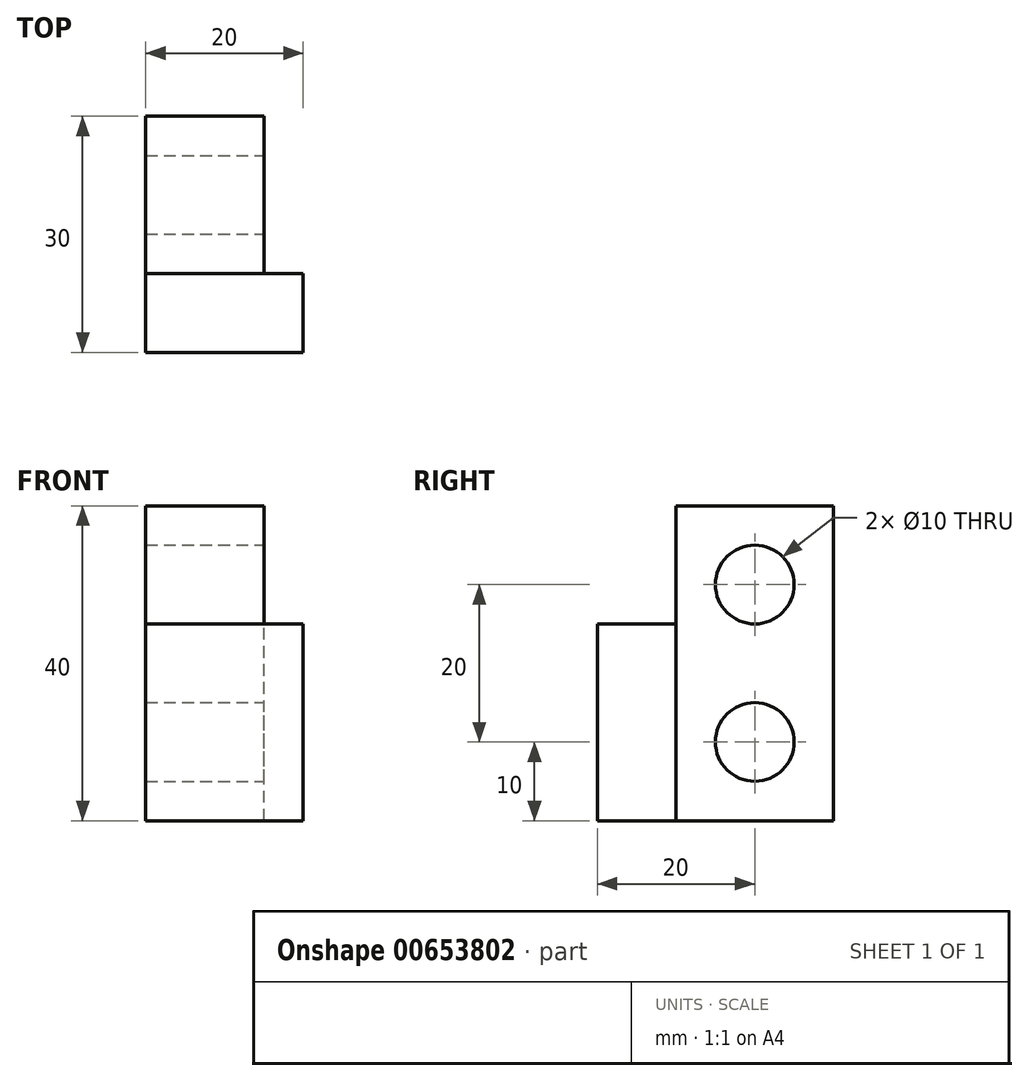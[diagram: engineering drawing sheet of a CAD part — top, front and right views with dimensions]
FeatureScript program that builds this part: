
annotation { "Feature Type Name" : "Feature", "Feature Type Description" : "" }
export const myFeature = defineFeature(function(context is Context, id is Id, definition is map)
    precondition{}
    {
        {
            var Q0;
            Q0=qCreatedBy(makeId("Right.planeOp"),FACE);
            var sketch = newSketch(context, id + "F0", { "sketchPlane" : qUnion([Q0])});
            skLineSegment(sketch, "E0.bottom", {"start": v(0, 0) * mm, "end": v(-20, 0) * mm});
            skLineSegment(sketch, "E0.top", {"start": v(0, 40) * mm, "end": v(-20, 40) * mm});
            skLineSegment(sketch, "E0.left", {"start": v(0, 0) * mm, "end": v(0, 40) * mm});
            skLineSegment(sketch, "E0.right", {"start": v(-20, 0) * mm, "end": v(-20, 40) * mm});
            skCircle(sketch, "E1", {"center": v(-10, 10) * mm, "radius": 5 * mm});
            skPoint(sketch, "E1.centerSnap0", {"position": v(-18.13, 10) * mm});
            skLineSegment(sketch, "E2.bottom", {"start": v(-20, 0) * mm, "end": v(-30, 0) * mm});
            skLineSegment(sketch, "E2.top", {"start": v(-20, 25) * mm, "end": v(-30, 25) * mm});
            skLineSegment(sketch, "E2.left", {"start": v(-20, 0) * mm, "end": v(-20, 25) * mm});
            skLineSegment(sketch, "E2.right", {"start": v(-30, 0) * mm, "end": v(-30, 25) * mm});
            skSolve(sketch);
        }
        {
            var Q0;
            Q0=makeQuery(id+"F0.imprint","IMPRINT",FACE,{"disambiguationData":[TD([[makeQuery(id+"F0.imprint","IMPRINT",EDGE,{"derivedFrom":sQuery(id+"F0.wireOp",EDGE,"E0.bottom")}),-1.0]])]});
            extrude(context, id + "F1", {"entities" : qUnion([Q0]), "depth" : 15 * mm, "offsetDistance" : 25.4 * mm});
        }
        {
            var Q0;
            Q0=makeQuery(id+"F0.imprint","IMPRINT",FACE,{"disambiguationData":[TD([[makeQuery(id+"F0.imprint","IMPRINT",EDGE,{"derivedFrom":sQuery(id+"F0.wireOp",EDGE,"E2.bottom")}),-1.0]])]});
            var Q1;
            Q1=makeQuery(id+"F0.imprint","IMPRINT",FACE,{"disambiguationData":[TD([[makeQuery(id+"F0.imprint","IMPRINT",EDGE,{"derivedFrom":sQuery(id+"F0.wireOp",EDGE,"E1")}),1.0]])]});
            extrude(context, id + "F2", {"entities" : qUnion([Q0, Q1]), "operationType" : NewBodyOperationType.ADD, "depth" : 20 * mm, "offsetDistance" : 25.4 * mm});
        }
        {
            var Q0;
            Q0=makeQuery(id+"F1.opExtrude","CAP_FACE",FACE,{"disambiguationData":[OSD([sQuery(id+"F0.wireOp",EDGE,"E0.bottom"),sQuery(id+"F0.wireOp",EDGE,"E0.top"),sQuery(id+"F0.wireOp",EDGE,"E0.left"),sQuery(id+"F0.wireOp",EDGE,"E0.right"),sQuery(id+"F0.wireOp",EDGE,"E1"),sQuery(id+"F0.wireOp",EDGE,"E2.left")])],"isStart":false});
            var sketch = newSketch(context, id + "F3", { "sketchPlane" : qUnion([Q0])});
            skCircle(sketch, "E3", {"center": v(-10, 30) * mm, "radius": 5 * mm});
            skSolve(sketch);
        }
        {
            var Q0;
            Q0=makeQuery(id+"F2.opExtrude","CAP_FACE",FACE,{"disambiguationData":[OSD([sQuery(id+"F0.wireOp",EDGE,"E1")])],"isStart":false});
            var Q1;
            {var subQ0=sQuery(id+"F0.wireOp",EDGE,"E2.left");var subQ1=sQuery(id+"F0.wireOp",EDGE,"E1");Q1=makeQuery(id+"F2.boolean.opBoolean","MERGE",FACE,{"derivedFrom":[makeQuery(id+"F1.opExtrude","CAP_FACE",FACE,{"disambiguationData":[OSD([sQuery(id+"F0.wireOp",EDGE,"E0.bottom"),sQuery(id+"F0.wireOp",EDGE,"E0.top"),sQuery(id+"F0.wireOp",EDGE,"E0.left"),sQuery(id+"F0.wireOp",EDGE,"E0.right"),subQ1,subQ0])],"isStart":true}),makeQuery(id+"F2.opExtrude","CAP_FACE",FACE,{"disambiguationData":[OSD([subQ1])],"isStart":true}),makeQuery(id+"F2.opExtrude","CAP_FACE",FACE,{"disambiguationData":[OSD([sQuery(id+"F0.wireOp",EDGE,"E2.bottom"),sQuery(id+"F0.wireOp",EDGE,"E2.top"),subQ0,sQuery(id+"F0.wireOp",EDGE,"E2.right")])],"isStart":true})]});}
            extrude(context, id + "F4", {"entities" : qUnion([Q0]), "operationType" : NewBodyOperationType.REMOVE, "endBound" : BoundingType.UP_TO_SURFACE, "oppositeDirection" : true, "depth" : 25.4 * mm, "endBoundEntityFace" : qUnion([Q1]), "offsetDistance" : 25.4 * mm});
        }
        {
            var Q0;
            Q0=makeQuery(id+"F3.imprint","IMPRINT",FACE,{"disambiguationData":[TD([[makeQuery(id+"F3.imprint","IMPRINT",EDGE,{"derivedFrom":sQuery(id+"F3.wireOp",EDGE,"E3")}),1.0]])]});
            var Q1;
            {var subQ0=sQuery(id+"F0.wireOp",EDGE,"E2.left");var subQ1=sQuery(id+"F0.wireOp",EDGE,"E1");Q1=makeQuery(id+"F2.boolean.opBoolean","MERGE",FACE,{"derivedFrom":[makeQuery(id+"F1.opExtrude","CAP_FACE",FACE,{"disambiguationData":[OSD([sQuery(id+"F0.wireOp",EDGE,"E0.bottom"),sQuery(id+"F0.wireOp",EDGE,"E0.top"),sQuery(id+"F0.wireOp",EDGE,"E0.left"),sQuery(id+"F0.wireOp",EDGE,"E0.right"),subQ1,subQ0])],"isStart":true}),makeQuery(id+"F2.opExtrude","CAP_FACE",FACE,{"disambiguationData":[OSD([subQ1])],"isStart":true}),makeQuery(id+"F2.opExtrude","CAP_FACE",FACE,{"disambiguationData":[OSD([sQuery(id+"F0.wireOp",EDGE,"E2.bottom"),sQuery(id+"F0.wireOp",EDGE,"E2.top"),subQ0,sQuery(id+"F0.wireOp",EDGE,"E2.right")])],"isStart":true})]});}
            extrude(context, id + "F5", {"entities" : qUnion([Q0]), "operationType" : NewBodyOperationType.REMOVE, "endBound" : BoundingType.UP_TO_SURFACE, "oppositeDirection" : true, "depth" : 25.4 * mm, "endBoundEntityFace" : qUnion([Q1]), "offsetDistance" : 25.4 * mm});
        }
    });
